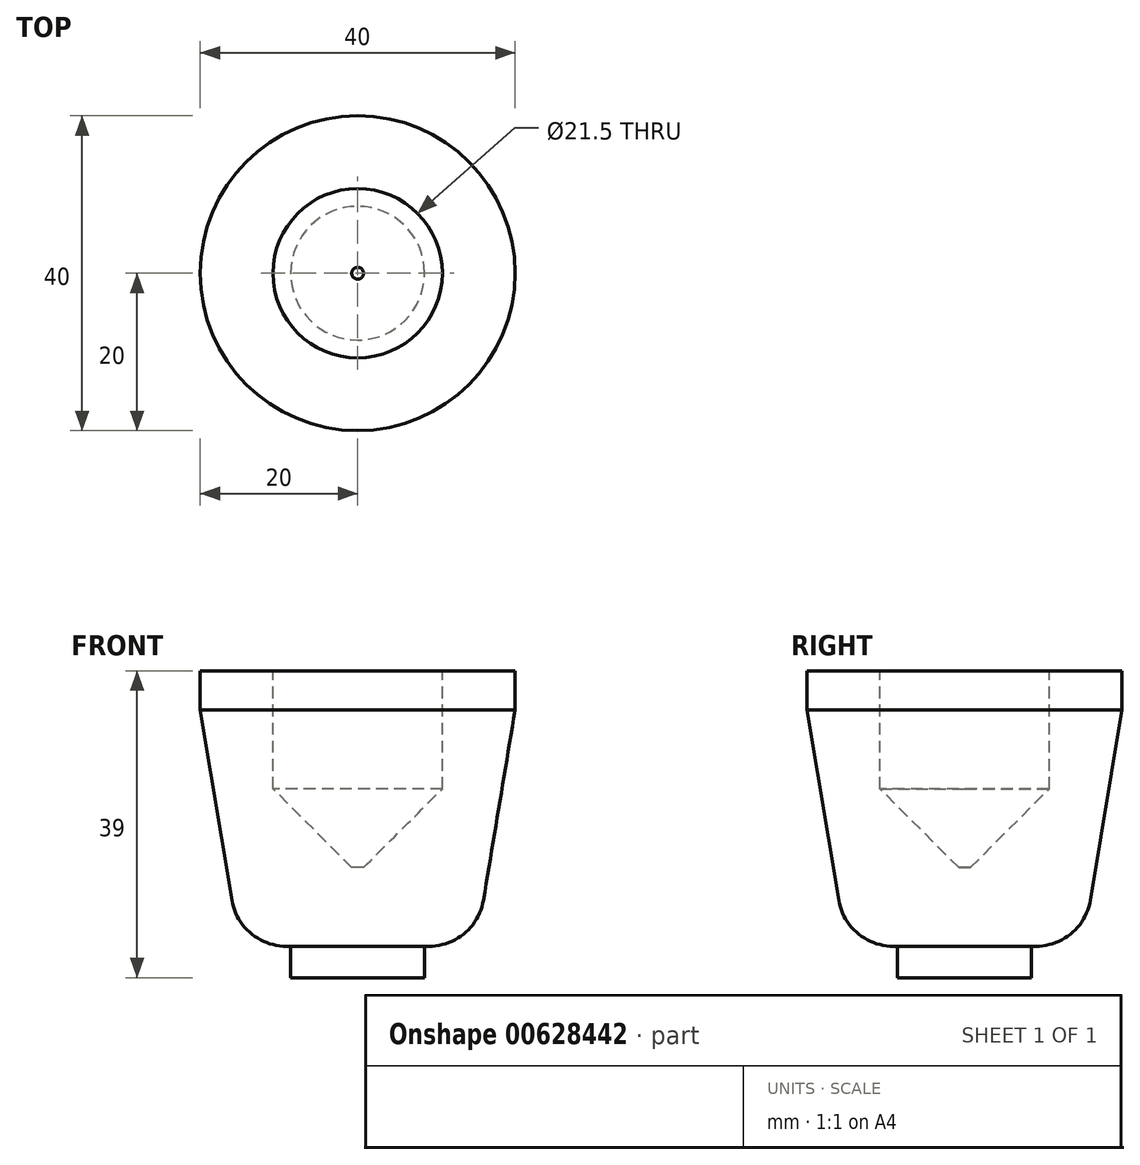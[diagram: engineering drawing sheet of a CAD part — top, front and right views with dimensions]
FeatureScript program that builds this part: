
annotation { "Feature Type Name" : "Feature", "Feature Type Description" : "" }
export const myFeature = defineFeature(function(context is Context, id is Id, definition is map)
    precondition{}
    {
        {
            var Q0;
            Q0=qCreatedBy(makeId("Top.planeOp"),FACE);
            var sketch = newSketch(context, id + "F0", { "sketchPlane" : qUnion([Q0])});
            skCircle(sketch, "E0", {"center": v(0, 0) * mm, "radius": 8.5 * mm});
            skSolve(sketch);
        }
        {
            var Q0;
            Q0 = qSketchRegion(id + "F0", true);
            extrude(context, id + "F1", {"entities" : qUnion([Q0]), "depth" : 4 * mm, "offsetDistance" : 25 * mm});
        }
        {
            var Q0;
            Q0=makeQuery(id+"F1.opExtrude","CAP_FACE",FACE,{"disambiguationData":[OSD([sQuery(id+"F0.wireOp",EDGE,"E0")])],"isStart":false});
            var sketch = newSketch(context, id + "F2", { "sketchPlane" : qUnion([Q0])});
            skCircle(sketch, "E1", {"center": v(0, 0) * mm, "radius": 20 * mm});
            skSolve(sketch);
        }
        {
            var Q0;
            Q0 = qSketchRegion(id + "F2", true);
            extrude(context, id + "F3", {"entities" : qUnion([Q0]), "operationType" : NewBodyOperationType.ADD, "depth" : 35 * mm, "offsetDistance" : 25 * mm});
        }
        {
            var Q0;
            Q0=makeQuery(id+"F3.opExtrude","CAP_EDGE",EDGE,{"disambiguationData":[OSD([sQuery(id+"F2.wireOp",EDGE,"E1")])],"isStart":true});
            chamfer(context, id + "F4", {"entities" : qUnion([Q0]), "chamferType" : ChamferType.TWO_OFFSETS, "width1" : 30 * mm, "oppositeDirection" : false, "width2" : 5 * mm, "tangentPropagation" : true});
        }
        {
            var Q0;
            {var subQ0=sQuery(id+"F2.wireOp",EDGE,"E1");Q0=makeQuery(id+"F4.opChamfer","BLEND_EDGE",EDGE,{"blendedFrom":[makeQuery(id+"F3.opExtrude","CAP_EDGE",EDGE,{"disambiguationData":[OSD([subQ0])],"isStart":true}),makeQuery(id+"F3.opExtrude","CAP_FACE",FACE,{"disambiguationData":[OSD([subQ0])],"isStart":true})],"blendedInto":[makeQuery(id+"F3.opExtrude","CAP_FACE",FACE,{"disambiguationData":[OSD([subQ0])],"isStart":true})]});}
            fillet(context, id + "F5", {"entities" : qUnion([Q0]), "radius" : 7 * mm, "tangentPropagation" : true, "allowEdgeOverflow" : false});
        }
        {
            var Q0;
            Q0=makeQuery(id+"F3.opExtrude","CAP_FACE",FACE,{"disambiguationData":[OSD([sQuery(id+"F2.wireOp",EDGE,"E1")])],"isStart":false});
            var sketch = newSketch(context, id + "F6", { "sketchPlane" : qUnion([Q0])});
            skCircle(sketch, "E2", {"center": v(0, 0) * mm, "radius": 10.75 * mm});
            skSolve(sketch);
        }
        {
            var Q0;
            Q0 = qSketchRegion(id + "F6", true);
            extrude(context, id + "F7", {"entities" : qUnion([Q0]), "operationType" : NewBodyOperationType.REMOVE, "oppositeDirection" : true, "depth" : 25 * mm, "offsetDistance" : 25 * mm});
        }
        {
            var Q0;
            Q0=makeQuery(id+"F7.boolean.opBoolean","COPY",EDGE,{"derivedFrom":makeQuery(id+"F7.opExtrude","CAP_EDGE",EDGE,{"disambiguationData":[OSD([sQuery(id+"F6.wireOp",EDGE,"E2")])],"isStart":false})});
            chamfer(context, id + "F8", {"entities" : qUnion([Q0]), "width" : 10 * mm, "tangentPropagation" : true});
        }
    });
